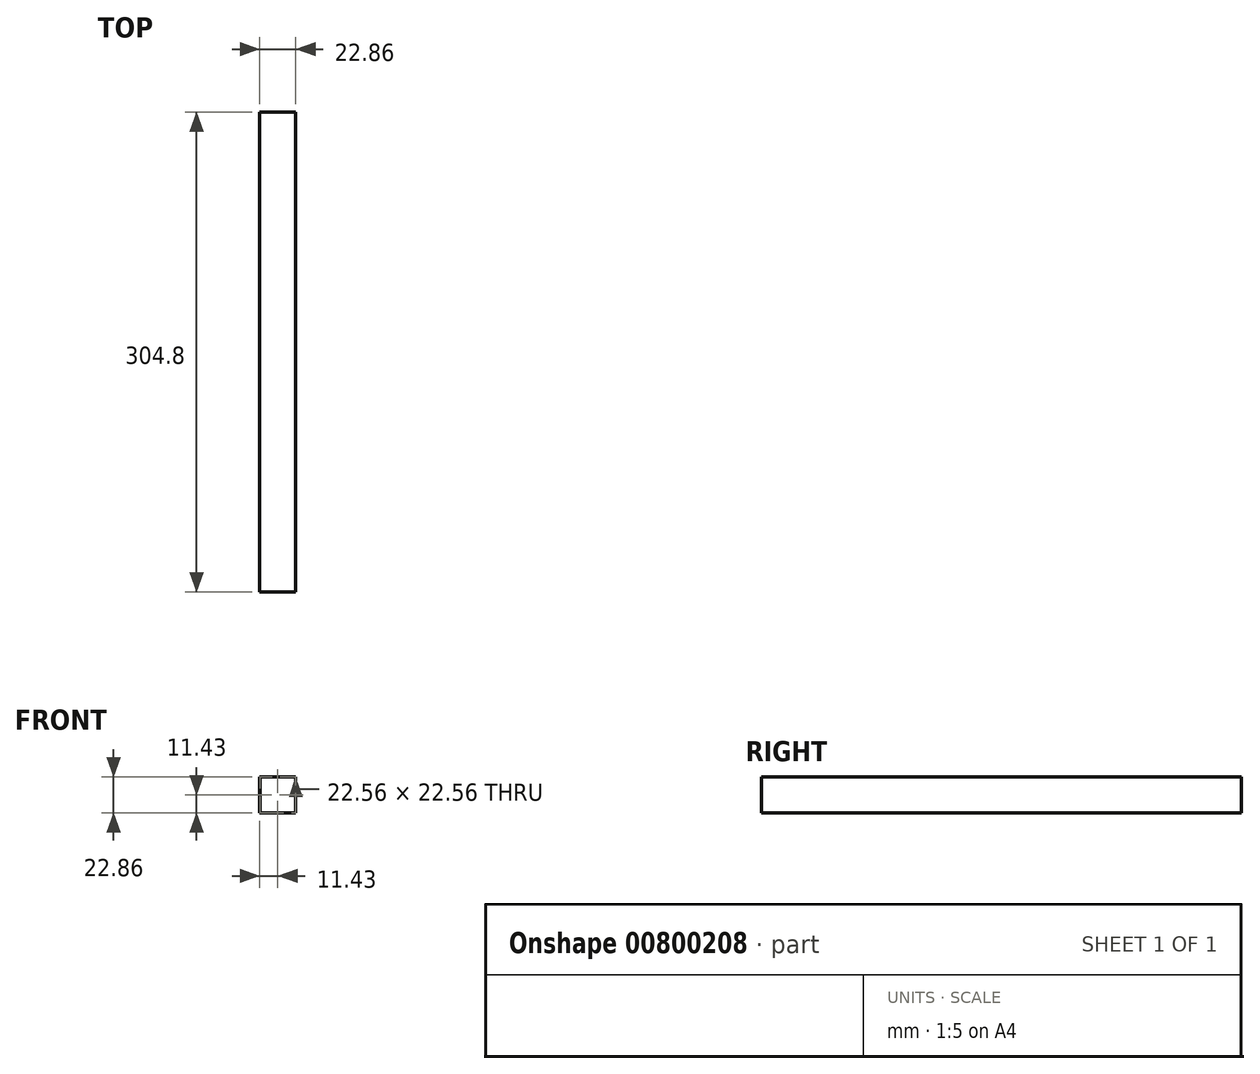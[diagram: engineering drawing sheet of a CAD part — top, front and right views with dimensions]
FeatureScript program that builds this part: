
annotation { "Feature Type Name" : "Feature", "Feature Type Description" : "" }
export const myFeature = defineFeature(function(context is Context, id is Id, definition is map)
    precondition{}
    {
        {
            var Q0;
            Q0=qCreatedBy(makeId("Front.planeOp"),FACE);
            var sketch = newSketch(context, id + "F0", { "sketchPlane" : qUnion([Q0])});
            skLineSegment(sketch, "E0.bottom", {"start": v(-11.43, 11.43) * mm, "end": v(11.43, 11.43) * mm});
            skLineSegment(sketch, "E0.top", {"start": v(-11.43, -11.43) * mm, "end": v(11.43, -11.43) * mm});
            skLineSegment(sketch, "E0.left", {"start": v(-11.43, 11.43) * mm, "end": v(-11.43, -11.43) * mm});
            skLineSegment(sketch, "E0.right", {"start": v(11.43, 11.43) * mm, "end": v(11.43, -11.43) * mm});
            skPoint(sketch, "E0.middle", {"position": v(0, 0) * mm});
            skLineSegment(sketch, "E1.bottom", {"start": v(-11.28, 11.28) * mm, "end": v(11.28, 11.28) * mm});
            skLineSegment(sketch, "E1.top", {"start": v(-11.28, -11.28) * mm, "end": v(11.28, -11.28) * mm});
            skLineSegment(sketch, "E1.left", {"start": v(-11.28, 11.28) * mm, "end": v(-11.28, -11.28) * mm});
            skLineSegment(sketch, "E1.right", {"start": v(11.28, 11.28) * mm, "end": v(11.28, -11.28) * mm});
            skSolve(sketch);
        }
        {
            var Q0;
            Q0 = qSketchRegion(id + "F0", true);
            extrude(context, id + "F1", {"entities" : qUnion([Q0]), "depth" : 304.8 * mm, "offsetDistance" : 25 * mm});
        }
    });
